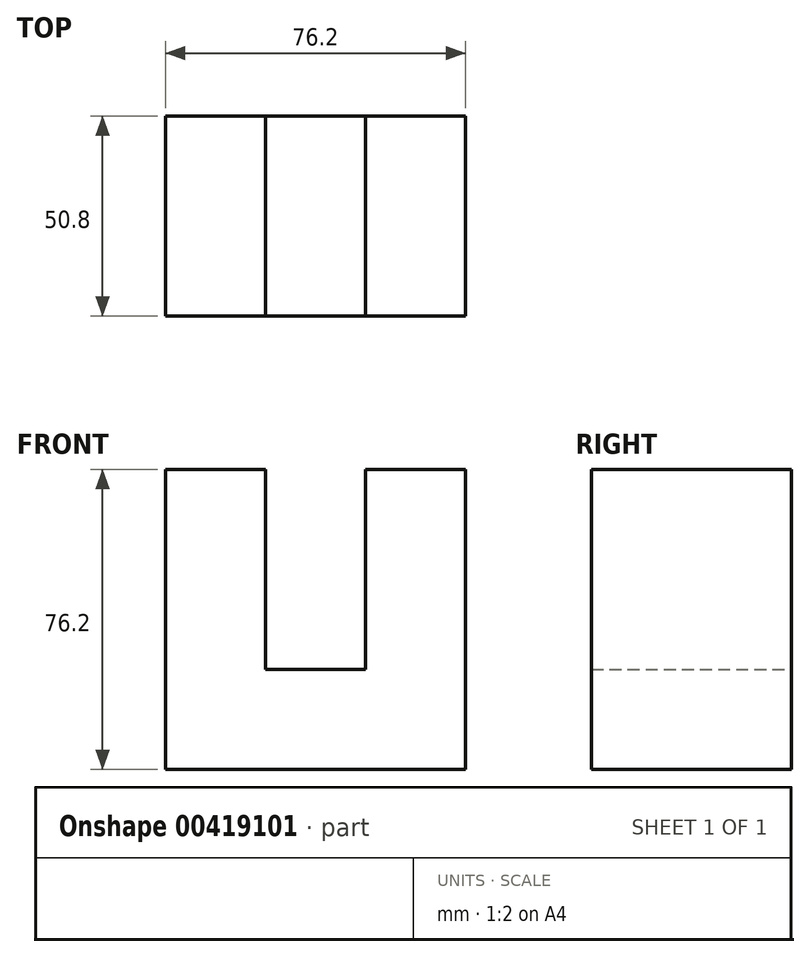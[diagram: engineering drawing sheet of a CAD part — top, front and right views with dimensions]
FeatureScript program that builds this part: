
annotation { "Feature Type Name" : "Feature", "Feature Type Description" : "" }
export const myFeature = defineFeature(function(context is Context, id is Id, definition is map)
    precondition{}
    {
        {
            var Q0;
            Q0=qCreatedBy(makeId("Front.planeOp"),FACE);
            var sketch = newSketch(context, id + "F0", { "sketchPlane" : qUnion([Q0])});
            skLineSegment(sketch, "E0", {"start": v(0, 0) * mm, "end": v(-76.2, 0) * mm});
            skLineSegment(sketch, "E1", {"start": v(0, 0) * mm, "end": v(0, 76.2) * mm});
            skLineSegment(sketch, "E2", {"start": v(-76.2, 0) * mm, "end": v(-76.2, 76.2) * mm});
            skLineSegment(sketch, "E3", {"start": v(-76.2, 76.2) * mm, "end": v(-50.8, 76.2) * mm});
            skLineSegment(sketch, "E4", {"start": v(-50.8, 76.2) * mm, "end": v(-50.8, 25.4) * mm});
            skLineSegment(sketch, "E5", {"start": v(-50.8, 25.4) * mm, "end": v(-25.4, 25.4) * mm});
            skLineSegment(sketch, "E6", {"start": v(-25.4, 25.4) * mm, "end": v(-25.4, 76.2) * mm});
            skLineSegment(sketch, "E7", {"start": v(-25.4, 76.2) * mm, "end": v(0, 76.2) * mm});
            skSolve(sketch);
        }
        {
            var Q0;
            Q0 = qSketchRegion(id + "F0", true);
            extrude(context, id + "F1", {"entities" : qUnion([Q0]), "depth" : 50.8 * mm});
        }
    });
